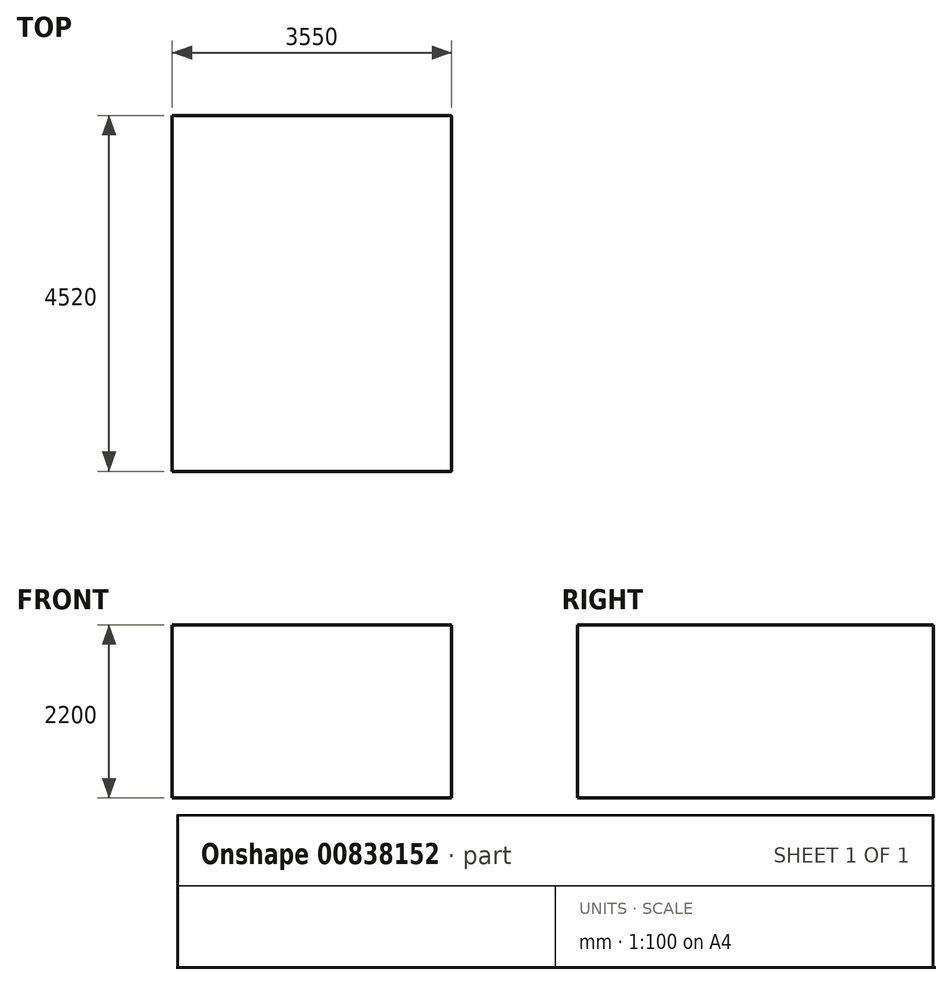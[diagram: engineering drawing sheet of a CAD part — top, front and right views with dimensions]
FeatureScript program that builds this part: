
annotation { "Feature Type Name" : "Feature", "Feature Type Description" : "" }
export const myFeature = defineFeature(function(context is Context, id is Id, definition is map)
    precondition{}
    {
        {
            var Q0;
            Q0=qCreatedBy(makeId("Top.planeOp"),FACE);
            var sketch = newSketch(context, id + "F0", { "sketchPlane" : qUnion([Q0])});
            skLineSegment(sketch, "E0.bottom", {"start": v(-1819.58, 2370.56) * mm, "end": v(1730.42, 2370.56) * mm});
            skLineSegment(sketch, "E0.top", {"start": v(-1819.58, -2149.44) * mm, "end": v(1730.42, -2149.44) * mm});
            skLineSegment(sketch, "E0.left", {"start": v(-1819.58, 2370.56) * mm, "end": v(-1819.58, -2149.44) * mm});
            skLineSegment(sketch, "E0.right", {"start": v(1730.42, 2370.56) * mm, "end": v(1730.42, -2149.44) * mm});
            skSolve(sketch);
        }
        {
            var Q0;
            Q0 = qSketchRegion(id + "F0", true);
            var Q1;
            Q1=makeQuery(id+"F0.imprint","IMPRINT",FACE,{"disambiguationData":[TD([[makeQuery(id+"F0.imprint","IMPRINT",EDGE,{"derivedFrom":sQuery(id+"F0.wireOp",EDGE,"E0.bottom")}),-1.0]])]});
            extrude(context, id + "F1", {"entities" : qUnion([Q0, Q1]), "depth" : 2200 * mm, "offsetDistance" : 25.4 * mm});
        }
    });
